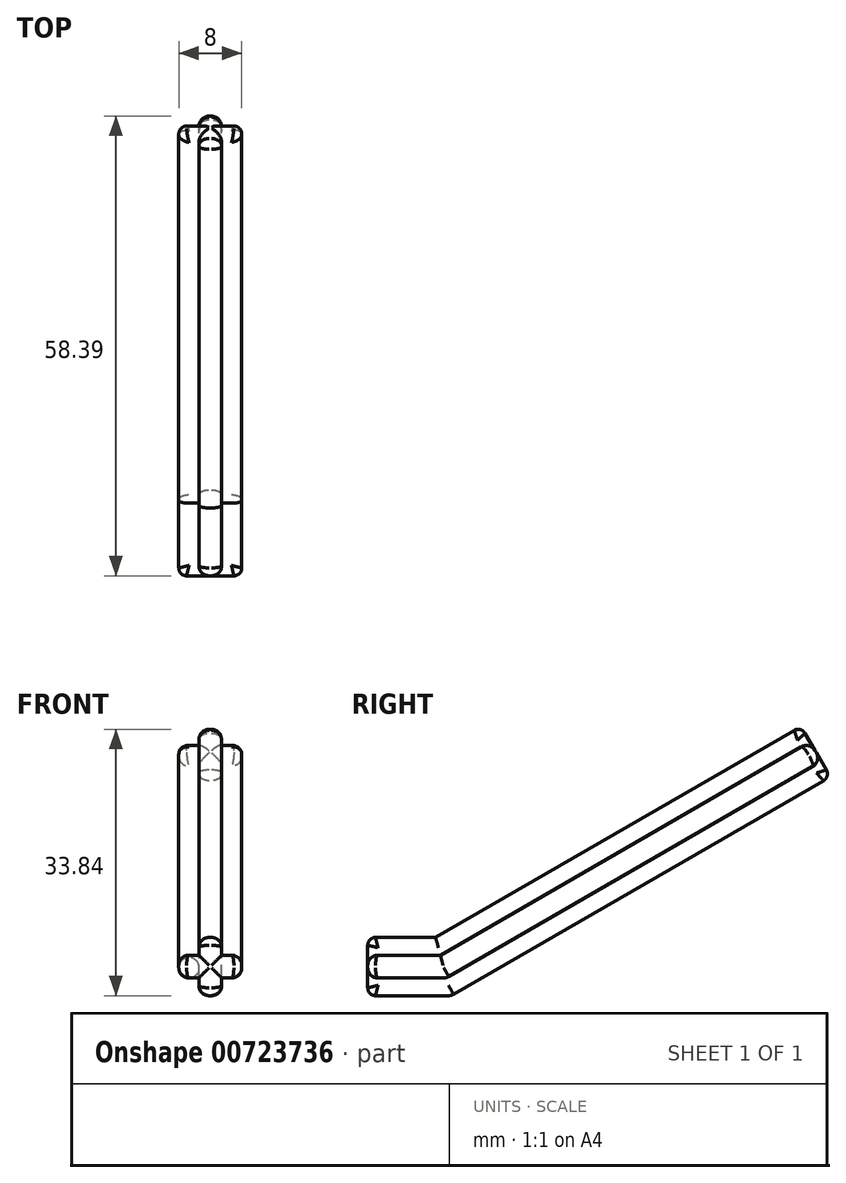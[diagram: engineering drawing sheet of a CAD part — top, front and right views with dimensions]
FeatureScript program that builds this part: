
annotation { "Feature Type Name" : "Feature", "Feature Type Description" : "" }
export const myFeature = defineFeature(function(context is Context, id is Id, definition is map)
    precondition{}
    {
        {
            var Q0;
            Q0=qCreatedBy(makeId("Front.planeOp"),FACE);
            var sketch = newSketch(context, id + "F0", { "sketchPlane" : qUnion([Q0]), "disableImprinting" : false});
            skLineSegment(sketch, "E0", {"start": v(-1.56, 5.15) * mm, "end": v(1.34, 5.15) * mm});
            skLineSegment(sketch, "E1", {"start": v(1.34, 5.15) * mm, "end": v(1.34, 2.9) * mm});
            skLineSegment(sketch, "E2", {"start": v(1.34, 2.9) * mm, "end": v(3.89, 2.9) * mm});
            skLineSegment(sketch, "E3", {"start": v(3.89, 2.9) * mm, "end": v(3.89, 0) * mm});
            skLineSegment(sketch, "E4", {"start": v(3.89, 0) * mm, "end": v(1.34, 0) * mm});
            skLineSegment(sketch, "E5", {"start": v(1.34, 0) * mm, "end": v(1.34, -2.25) * mm});
            skLineSegment(sketch, "E6", {"start": v(1.34, -2.25) * mm, "end": v(-1.56, -2.25) * mm});
            skLineSegment(sketch, "E7", {"start": v(-1.56, -2.25) * mm, "end": v(-1.56, 0) * mm});
            skLineSegment(sketch, "E8", {"start": v(-1.56, 0) * mm, "end": v(-4.11, 0) * mm});
            skLineSegment(sketch, "E9", {"start": v(-4.11, 0) * mm, "end": v(-4.11, 2.9) * mm});
            skLineSegment(sketch, "E10", {"start": v(-4.11, 2.9) * mm, "end": v(-1.56, 2.9) * mm});
            skLineSegment(sketch, "E11", {"start": v(-1.56, 2.9) * mm, "end": v(-1.56, 5.15) * mm});
            skSolve(sketch);
        }
        {
            var Q0;
            Q0=makeQuery(id+"F0.imprint","IMPRINT",FACE,{"disambiguationData":[TD([[makeQuery(id+"F0.imprint","IMPRINT",EDGE,{"derivedFrom":sQuery(id+"F0.wireOp",EDGE,"UtKreHIs-wQzj-hOnl-QTd2-efQIdA6IQ0sK.bottom")}),-1.0]])]});
            var Q1;
            Q1=makeQuery(id+"F0.imprint","IMPRINT",FACE,{"disambiguationData":[TD([[makeQuery(id+"F0.imprint","IMPRINT",EDGE,{"derivedFrom":sQuery(id+"F0.wireOp",EDGE,"vfKRYdqZ-3U3v-tKmi-eyxM-GFFEIJJJ27wv.bottom")}),-1.0]])]});
            var Q2;
            Q2 = qSketchRegion(id + "F0", true);
            extrude(context, id + "F1", {"entities" : qUnion([Q0, Q1, Q2]), "flatOperationType" : FlatOperationType.REMOVE, "depth" : -5 * mm, "offsetDistance" : 25 * mm, "domain" : OperationDomain.MODEL});
        }
        {
            var Q0;
            Q0=qCreatedBy(makeId("Right.planeOp"),FACE);
            var sketch = newSketch(context, id + "F2", { "sketchPlane" : qUnion([Q0]), "disableImprinting" : false});
            skLineSegment(sketch, "E12", {"start": v(0, 0) * mm, "end": v(10, 0) * mm});
            skLineSegment(sketch, "E13", {"start": v(10, 0) * mm, "end": v(57.63, 27.5) * mm});
            skSolve(sketch);
        }
        {
            var Q0;
            Q0 = qSketchRegion(id + "F0", true);
            var Q1;
            Q1=sQuery(id+"F2.wireOp",EDGE,"E13");
            var Q2;
            Q2=sQuery(id+"F2.wireOp",EDGE,"E12");
            sweep(context, id + "F3", {"operationType" : NewBodyOperationType.ADD, "profiles" : qUnion([Q0]), "path" : qUnion([Q1, Q2])});
        }
        {
            var Q0;
            Q0=makeQuery(id+"F1.opExtrude","CAP_EDGE",EDGE,{"disambiguationData":[OSD([sQuery(id+"F0.wireOp",EDGE,"E3")])],"isStart":true});
            var Q1;
            Q1=makeQuery(id+"F1.opExtrude","CAP_EDGE",EDGE,{"disambiguationData":[OSD([sQuery(id+"F0.wireOp",EDGE,"E9")])],"isStart":true});
            var Q2;
            Q2=makeQuery(id+"F1.opExtrude","CAP_EDGE",EDGE,{"disambiguationData":[OSD([sQuery(id+"F0.wireOp",EDGE,"E6")])],"isStart":true});
            var Q3;
            Q3=makeQuery(id+"F1.opExtrude","CAP_EDGE",EDGE,{"disambiguationData":[OSD([sQuery(id+"F0.wireOp",EDGE,"E0")])],"isStart":true});
            fillet(context, id + "F4", {"entities" : qUnion([Q0, Q1, Q2, Q3]), "radius" : 1 * mm, "width" : 5 * mm, "tangentPropagation" : true, "blendControlType" : BlendControlType.RADIUS, "defaultsChanged" : false, "vertexSettings" : [], "pointOnEdgeSettings" : [], "allowEdgeOverflow" : false, "smoothCorners" : false, "filletType" : FilletType.EDGE});
        }
        {
            var Q0;
            Q0=makeQuery(id+"F3.opSweep","CAP_EDGE",EDGE,{"disambiguationData":[OSD([sQuery(id+"F0.wireOp",EDGE,"E9"),sQuery(id+"F2.wireOp",VERTEX,"E13.end")])],"isStart":false});
            var Q1;
            Q1=makeQuery(id+"F3.opSweep","CAP_EDGE",EDGE,{"disambiguationData":[OSD([sQuery(id+"F0.wireOp",EDGE,"E6"),sQuery(id+"F2.wireOp",VERTEX,"E13.end")])],"isStart":false});
            var Q2;
            Q2=makeQuery(id+"F3.opSweep","CAP_EDGE",EDGE,{"disambiguationData":[OSD([sQuery(id+"F0.wireOp",EDGE,"E3"),sQuery(id+"F2.wireOp",VERTEX,"E13.end")])],"isStart":false});
            var Q3;
            Q3=makeQuery(id+"F3.opSweep","CAP_EDGE",EDGE,{"disambiguationData":[OSD([sQuery(id+"F0.wireOp",EDGE,"E0"),sQuery(id+"F2.wireOp",VERTEX,"E13.end")])],"isStart":false});
            fillet(context, id + "F5", {"entities" : qUnion([Q0, Q1, Q2, Q3]), "radius" : 1 * mm, "tangentPropagation" : true, "allowEdgeOverflow" : false});
        }
        {
            var Q0;
            Q0=makeQuery(id+"F3.opSweep","SWEPT_EDGE",EDGE,{"disambiguationData":[OSD([sQuery(id+"F0.wireOp",EDGE,"E0"),sQuery(id+"F0.wireOp",EDGE,"E11"),sQuery(id+"F2.wireOp",EDGE,"E13")])]});
            var Q1;
            Q1=makeQuery(id+"F3.opSweep","SWEPT_EDGE",EDGE,{"disambiguationData":[OSD([sQuery(id+"F0.wireOp",EDGE,"E9"),sQuery(id+"F0.wireOp",EDGE,"E10"),sQuery(id+"F2.wireOp",EDGE,"E13")])]});
            var Q2;
            Q2=makeQuery(id+"F3.opSweep","SWEPT_EDGE",EDGE,{"disambiguationData":[OSD([sQuery(id+"F0.wireOp",EDGE,"E8"),sQuery(id+"F0.wireOp",EDGE,"E9"),sQuery(id+"F2.wireOp",EDGE,"E13")])]});
            var Q3;
            Q3=makeQuery(id+"F3.opSweep","SWEPT_EDGE",EDGE,{"disambiguationData":[OSD([sQuery(id+"F0.wireOp",EDGE,"E6"),sQuery(id+"F0.wireOp",EDGE,"E7"),sQuery(id+"F2.wireOp",EDGE,"E13")])]});
            var Q4;
            Q4=makeQuery(id+"F3.opSweep","SWEPT_EDGE",EDGE,{"disambiguationData":[OSD([sQuery(id+"F0.wireOp",EDGE,"E0"),sQuery(id+"F0.wireOp",EDGE,"E1"),sQuery(id+"F2.wireOp",EDGE,"E13")])]});
            var Q5;
            Q5=makeQuery(id+"F3.opSweep","SWEPT_EDGE",EDGE,{"disambiguationData":[OSD([sQuery(id+"F0.wireOp",EDGE,"E2"),sQuery(id+"F0.wireOp",EDGE,"E3"),sQuery(id+"F2.wireOp",EDGE,"E13")])]});
            var Q6;
            Q6=makeQuery(id+"F3.opSweep","SWEPT_EDGE",EDGE,{"disambiguationData":[OSD([sQuery(id+"F0.wireOp",EDGE,"E3"),sQuery(id+"F0.wireOp",EDGE,"E4"),sQuery(id+"F2.wireOp",EDGE,"E13")])]});
            var Q7;
            Q7=makeQuery(id+"F3.opSweep","SWEPT_EDGE",EDGE,{"disambiguationData":[OSD([sQuery(id+"F0.wireOp",EDGE,"E5"),sQuery(id+"F0.wireOp",EDGE,"E6"),sQuery(id+"F2.wireOp",EDGE,"E13")])]});
            fillet(context, id + "F6", {"entities" : qUnion([Q0, Q1, Q2, Q3, Q4, Q5, Q6, Q7]), "radius" : 1.3 * mm, "tangentPropagation" : true, "allowEdgeOverflow" : false});
        }
        {
            var Q0;
            {var subQ0=sQuery(id+"F0.wireOp",EDGE,"E1");var subQ1=sQuery(id+"F0.wireOp",EDGE,"E0");Q0=makeQuery(id+"F3.boolean.opBoolean","MERGE",EDGE,{"derivedFrom":[makeQuery(id+"F1.opExtrude","SWEPT_EDGE",EDGE,{"disambiguationData":[OSD([subQ1,subQ0])]}),makeQuery(id+"F3.opSweep","SWEPT_EDGE",EDGE,{"disambiguationData":[OSD([subQ1,subQ0,sQuery(id+"F2.wireOp",EDGE,"E12")])]})]});}
            var Q1;
            {var subQ0=sQuery(id+"F0.wireOp",EDGE,"E11");var subQ1=sQuery(id+"F0.wireOp",EDGE,"E0");Q1=makeQuery(id+"F3.boolean.opBoolean","MERGE",EDGE,{"derivedFrom":[makeQuery(id+"F1.opExtrude","SWEPT_EDGE",EDGE,{"disambiguationData":[OSD([subQ1,subQ0])]}),makeQuery(id+"F3.opSweep","SWEPT_EDGE",EDGE,{"disambiguationData":[OSD([subQ1,subQ0,sQuery(id+"F2.wireOp",EDGE,"E12")])]})]});}
            var Q2;
            {var subQ0=sQuery(id+"F0.wireOp",EDGE,"E3");var subQ1=sQuery(id+"F0.wireOp",EDGE,"E2");Q2=makeQuery(id+"F3.boolean.opBoolean","MERGE",EDGE,{"derivedFrom":[makeQuery(id+"F1.opExtrude","SWEPT_EDGE",EDGE,{"disambiguationData":[OSD([subQ1,subQ0])]}),makeQuery(id+"F3.opSweep","SWEPT_EDGE",EDGE,{"disambiguationData":[OSD([subQ1,subQ0,sQuery(id+"F2.wireOp",EDGE,"E12")])]})]});}
            var Q3;
            {var subQ0=sQuery(id+"F0.wireOp",EDGE,"E4");var subQ1=sQuery(id+"F0.wireOp",EDGE,"E3");Q3=makeQuery(id+"F3.boolean.opBoolean","MERGE",EDGE,{"derivedFrom":[makeQuery(id+"F1.opExtrude","SWEPT_EDGE",EDGE,{"disambiguationData":[OSD([subQ1,subQ0])]}),makeQuery(id+"F3.opSweep","SWEPT_EDGE",EDGE,{"disambiguationData":[OSD([subQ1,subQ0,sQuery(id+"F2.wireOp",EDGE,"E12")])]})]});}
            var Q4;
            {var subQ0=sQuery(id+"F0.wireOp",EDGE,"E6");var subQ1=sQuery(id+"F0.wireOp",EDGE,"E5");Q4=makeQuery(id+"F3.boolean.opBoolean","MERGE",EDGE,{"derivedFrom":[makeQuery(id+"F1.opExtrude","SWEPT_EDGE",EDGE,{"disambiguationData":[OSD([subQ1,subQ0])]}),makeQuery(id+"F3.opSweep","SWEPT_EDGE",EDGE,{"disambiguationData":[OSD([subQ1,subQ0,sQuery(id+"F2.wireOp",EDGE,"E12")])]})]});}
            var Q5;
            {var subQ0=sQuery(id+"F0.wireOp",EDGE,"E9");var subQ1=sQuery(id+"F0.wireOp",EDGE,"E8");Q5=makeQuery(id+"F3.boolean.opBoolean","MERGE",EDGE,{"derivedFrom":[makeQuery(id+"F1.opExtrude","SWEPT_EDGE",EDGE,{"disambiguationData":[OSD([subQ1,subQ0])]}),makeQuery(id+"F3.opSweep","SWEPT_EDGE",EDGE,{"disambiguationData":[OSD([subQ1,subQ0,sQuery(id+"F2.wireOp",EDGE,"E12")])]})]});}
            var Q6;
            {var subQ0=sQuery(id+"F0.wireOp",EDGE,"E10");var subQ1=sQuery(id+"F0.wireOp",EDGE,"E9");Q6=makeQuery(id+"F3.boolean.opBoolean","MERGE",EDGE,{"derivedFrom":[makeQuery(id+"F1.opExtrude","SWEPT_EDGE",EDGE,{"disambiguationData":[OSD([subQ1,subQ0])]}),makeQuery(id+"F3.opSweep","SWEPT_EDGE",EDGE,{"disambiguationData":[OSD([subQ1,subQ0,sQuery(id+"F2.wireOp",EDGE,"E12")])]})]});}
            fillet(context, id + "F7", {"entities" : qUnion([Q0, Q1, Q2, Q3, Q4, Q5, Q6]), "radius" : 1.3 * mm, "tangentPropagation" : true, "allowEdgeOverflow" : false});
        }
    });
